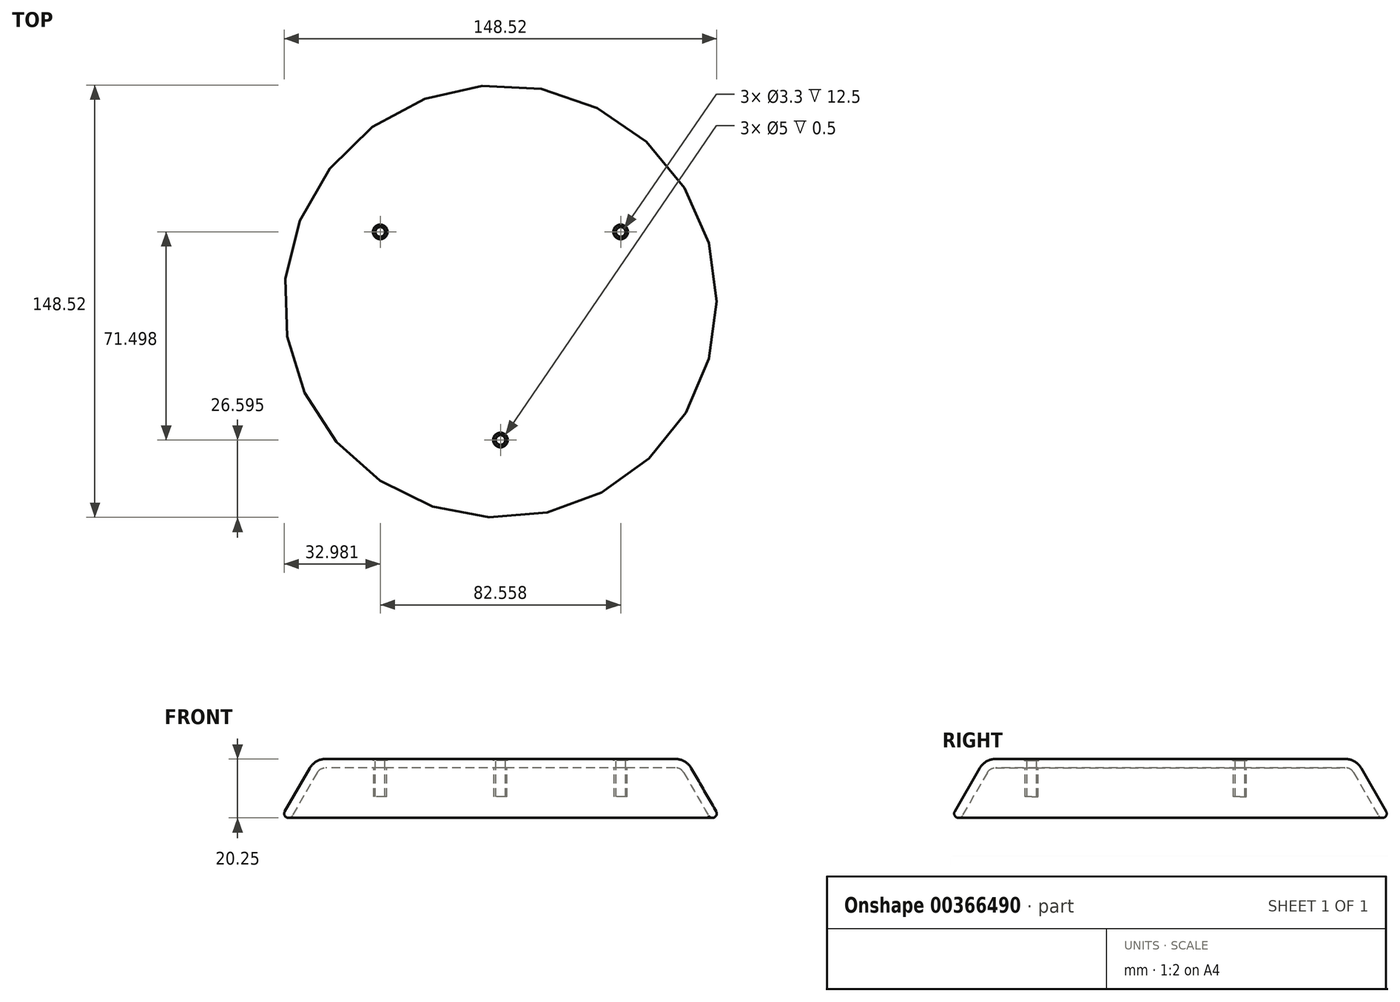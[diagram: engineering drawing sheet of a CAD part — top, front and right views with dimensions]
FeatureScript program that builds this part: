
annotation { "Feature Type Name" : "Feature", "Feature Type Description" : "" }
export const myFeature = defineFeature(function(context is Context, id is Id, definition is map)
    precondition{}
    {
        {
            var Q0;
            Q0=qCreatedBy(makeId("Front.planeOp"),FACE);
            var sketch = newSketch(context, id + "F0", { "sketchPlane" : qUnion([Q0])});
            skLineSegment(sketch, "E0", {"start": v(0, 18) * mm, "end": v(-60, 18) * mm});
            skLineSegment(sketch, "E1", {"start": v(-65.5, 14.82) * mm, "end": v(-74.06, 0) * mm});
            skPoint(sketch, "E2.visualSharp", {"position": v(-63.67, 18) * mm});
            skArc(sketch, "E2.filletArc", {"start": v(-60, 18) * mm, "mid": v(-63.17, 17.15) * mm, "end": v(-65.5, 14.82) * mm});
            skLineSegment(sketch, "E3.0", {"start": v(-62.9, 13.33) * mm, "end": v(-71.46, -1.5) * mm});
            skArc(sketch, "E3.1", {"start": v(-60, 15) * mm, "mid": v(-61.68, 14.55) * mm, "end": v(-62.9, 13.33) * mm});
            skLineSegment(sketch, "E3.2", {"start": v(0, 15) * mm, "end": v(-60, 15) * mm});
            skArc(sketch, "E4", {"start": v(-74.06, 0) * mm, "mid": v(-73.5, -2.05) * mm, "end": v(-71.46, -1.5) * mm});
            skLineSegment(sketch, "E5", {"start": v(0, 18) * mm, "end": v(0, 15) * mm});
            skSolve(sketch);
        }
        {
            var Q0;
            Q0 = qSketchRegion(id + "F0", true);
            var Q1;
            Q1=sQuery(id+"F0.wireOp",EDGE,"E5");
            revolve(context, id + "F1", {"entities" : qUnion([Q0]), "axis" : qUnion([Q1]), "revolveType" : RevolveType.FULL});
        }
        {
            var Q0;
            Q0=makeQuery(id+"F1.opRevolve","SWEPT_FACE",FACE,{"disambiguationData":[OSD([sQuery(id+"F0.wireOp",EDGE,"E3.2")])]});
            var sketch = newSketch(context, id + "F2", { "sketchPlane" : qUnion([Q0])});
            skCircle(sketch, "E6", {"center": v(0, 47.67) * mm, "radius": 1.65 * mm});
            skCircle(sketch, "E7", {"center": v(0, 47.67) * mm, "radius": 2.25 * mm});
            skCircle(sketch, "E8.1.0", {"center": v(-41.28, -23.83) * mm, "radius": 2.25 * mm});
            skCircle(sketch, "E8.1.1", {"center": v(-41.28, -23.83) * mm, "radius": 1.65 * mm});
            skCircle(sketch, "E8.2.0", {"center": v(41.28, -23.83) * mm, "radius": 2.25 * mm});
            skCircle(sketch, "E8.2.1", {"center": v(41.28, -23.83) * mm, "radius": 1.65 * mm});
            skPoint(sketch, "E8.center", {"position": v(0, 0) * mm});
            skSolve(sketch);
        }
        {
            var Q0;
            Q0 = qSketchRegion(id + "F2", true);
            extrude(context, id + "F3", {"entities" : qUnion([Q0]), "operationType" : NewBodyOperationType.ADD, "depth" : 10 * mm});
        }
        {
            var Q0;
            Q0=makeQuery(id+"F3.boolean.opBoolean","SPLIT",FACE,{"disambiguationData":[TD([makeQuery(id+"F1.opRevolve","SWEPT_FACE",FACE,{"disambiguationData":[OSD([sQuery(id+"F0.wireOp",EDGE,"E3.1")])]})])],"derivedFrom":makeQuery(id+"F1.opRevolve","SWEPT_FACE",FACE,{"disambiguationData":[OSD([sQuery(id+"F0.wireOp",EDGE,"E3.2")])]})});
            var sketch = newSketch(context, id + "F4", { "sketchPlane" : qUnion([Q0])});
            skCircle(sketch, "E9", {"center": v(0, 47.67) * mm, "radius": 1.65 * mm});
            skCircle(sketch, "E10", {"center": v(-41.28, -23.83) * mm, "radius": 1.65 * mm});
            skCircle(sketch, "E11", {"center": v(41.28, -23.83) * mm, "radius": 1.65 * mm});
            skSolve(sketch);
        }
        {
            var Q0;
            Q0 = qSketchRegion(id + "F4", true);
            extrude(context, id + "F5", {"entities" : qUnion([Q0]), "operationType" : NewBodyOperationType.REMOVE, "oppositeDirection" : true, "depth" : 3 * mm});
        }
        {
            var Q0;
            Q0=makeQuery(id+"F1.opRevolve","SWEPT_FACE",FACE,{"disambiguationData":[OSD([sQuery(id+"F0.wireOp",EDGE,"E0")])]});
            var sketch = newSketch(context, id + "F6", { "sketchPlane" : qUnion([Q0])});
            skCircle(sketch, "E12", {"center": v(0, -47.67) * mm, "radius": 2.5 * mm});
            skCircle(sketch, "E13", {"center": v(41.28, 23.83) * mm, "radius": 2.5 * mm});
            skCircle(sketch, "E14", {"center": v(-41.28, 23.83) * mm, "radius": 2.5 * mm});
            skSolve(sketch);
        }
        {
            var Q0;
            Q0 = qSketchRegion(id + "F6", true);
            extrude(context, id + "F7", {"entities" : qUnion([Q0]), "operationType" : NewBodyOperationType.REMOVE, "oppositeDirection" : true, "depth" : .5 * mm});
        }
    });
